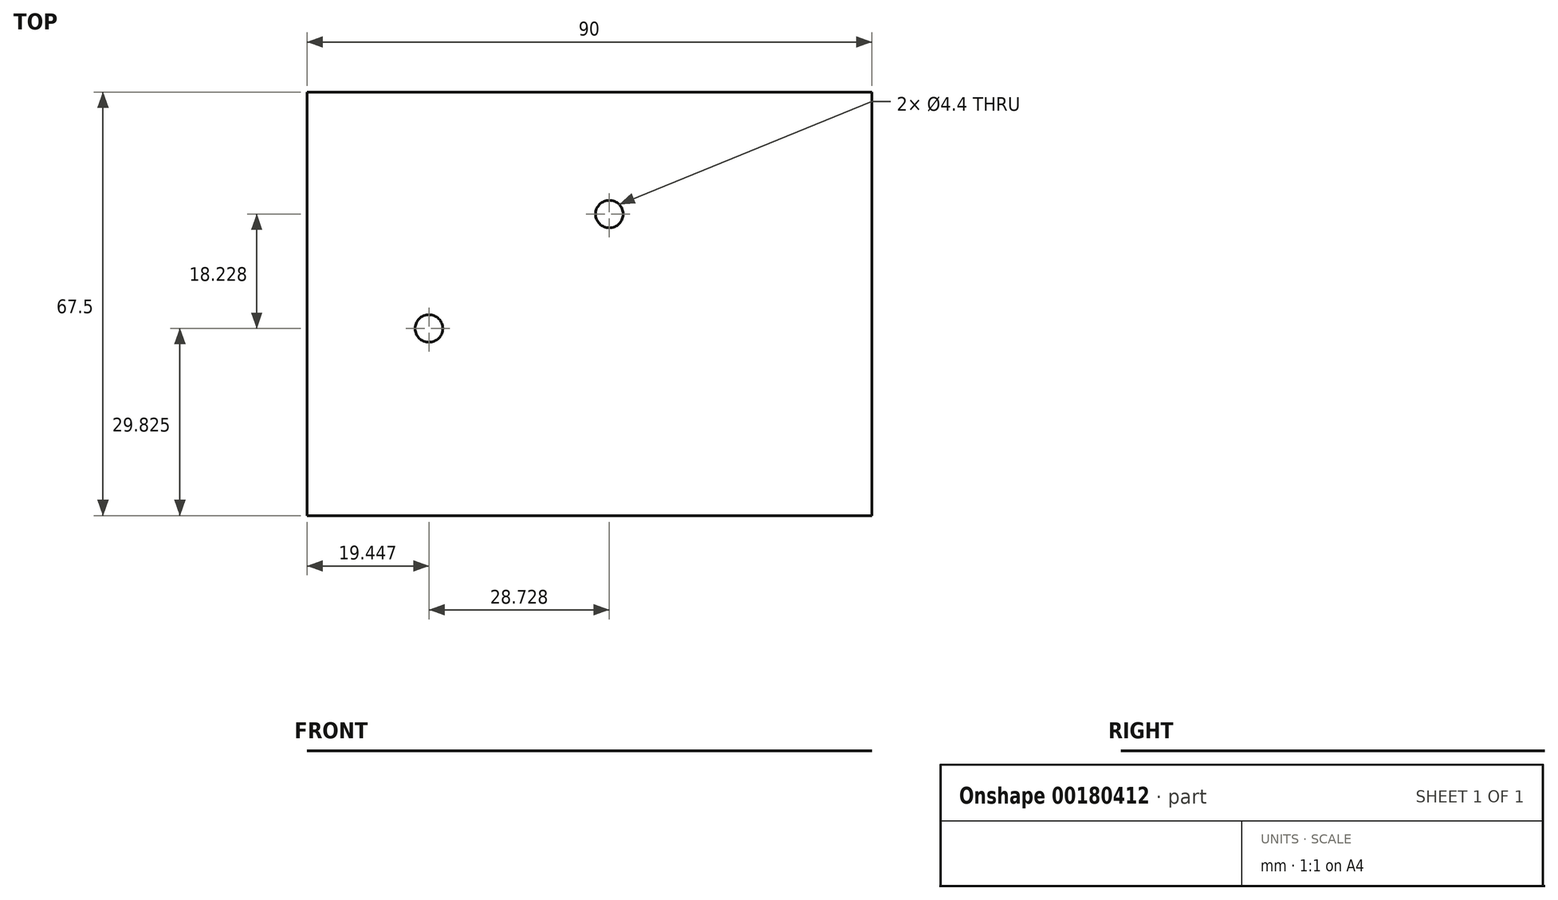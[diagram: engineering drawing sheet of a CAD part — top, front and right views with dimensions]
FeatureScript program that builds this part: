
annotation { "Feature Type Name" : "Feature", "Feature Type Description" : "" }
export const myFeature = defineFeature(function(context is Context, id is Id, definition is map)
    precondition{}
    {
        {
            var Q0;
            Q0=qCreatedBy(makeId("Top.planeOp"),FACE);
            var sketch = newSketch(context, id + "F0", { "sketchPlane" : qUnion([Q0])});
            skLineSegment(sketch, "E0.bottom", {"start": v(45, -33.75) * mm, "end": v(-45, -33.75) * mm});
            skLineSegment(sketch, "E0.top", {"start": v(45, 33.75) * mm, "end": v(-45, 33.75) * mm});
            skLineSegment(sketch, "E0.left", {"start": v(45, -33.75) * mm, "end": v(45, 33.75) * mm});
            skLineSegment(sketch, "E0.right", {"start": v(-45, -33.75) * mm, "end": v(-45, 33.75) * mm});
            skPoint(sketch, "E0.middle", {"position": v(0, 0) * mm});
            skSolve(sketch);
        }
        {
            var Q0;
            Q0=makeQuery(id+"F0.imprint","IMPRINT",FACE,{"disambiguationData":[TD([[makeQuery(id+"F0.imprint","IMPRINT",EDGE,{"derivedFrom":sQuery(id+"F0.wireOp",EDGE,"E0.bottom")}),-1.0]])]});
            extrude(context, id + "F1", {"entities" : qUnion([Q0]), "depth" : 1 / 203.2 * mm});
        }
        {
            var Q0;
            Q0=makeQuery(id+"F1.opExtrude","CAP_FACE",FACE,{"disambiguationData":[OSD([sQuery(id+"F0.wireOp",EDGE,"E0.bottom"),sQuery(id+"F0.wireOp",EDGE,"E0.top"),sQuery(id+"F0.wireOp",EDGE,"E0.left"),sQuery(id+"F0.wireOp",EDGE,"E0.right")])],"isStart":false});
            var sketch = newSketch(context, id + "F2", { "sketchPlane" : qUnion([Q0])});
            skPoint(sketch, "E1", {"position": v(3.17, 14.3) * mm});
            skPoint(sketch, "E2", {"position": v(-25.55, -3.93) * mm});
            skPoint(sketch, "E3", {"position": v(-45, 0) * mm});
            skSolve(sketch);
        }
        {
            var Q0;
            Q0=sQuery(id+"F2.wireOp",VERTEX,"E2");
            var Q1;
            Q1=sQuery(id+"F2.wireOp",VERTEX,"E1");
            var Q2;
            Q2=makeQuery(id+"F1.opExtrude","SWEPT_BODY",BODY,{"disambiguationData":[OSD([sQuery(id+"F0.wireOp",EDGE,"E0.bottom"),sQuery(id+"F0.wireOp",EDGE,"E0.top"),sQuery(id+"F0.wireOp",EDGE,"E0.left"),sQuery(id+"F0.wireOp",EDGE,"E0.right")])]});
            hole(context, id + "F3", {"style" : HoleStyle.SIMPLE, "endStyle" : HoleEndStyle.THROUGH, "standardTappedOrClearance" : lookupTablePath({ "standard" : "ISO", "fit" : "Normal", "size" : "M4", "type" : "Clearance" }), "standardBlindInLast" : lookupTablePath({ "fit" : "Standard", "standard" : "ISO", "size" : "M4", "type" : "Clearance" }), "holeDiameter" : 4.4 * mm, "locations" : qUnion([Q0, Q1]), "scope" : qUnion([Q2]), "isTappedThrough" : true});
        }
    });
